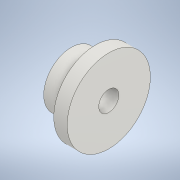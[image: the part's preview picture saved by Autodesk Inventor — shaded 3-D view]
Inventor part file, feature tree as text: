
AUTODESK INVENTOR PART (.ipt)
format: ipt  version: 2022.1 (Build 261234000, 234)  size: 116,224 bytes
history: native  units: mm
features: extrude x3, sketch x3
ambient origin geometry x8: Origin, YZ Plane, XZ Plane, XY Plane, X Axis, Y Axis, Z Axis, Center Point
bodies: Body1 (feature_tree)
feature tree (6):
  extrude  "Extrusión3"  Depth=28.0mm TaperAngle=0.0deg
  extrude  "Extrusión4"  Depth=18.0mm TaperAngle=0.0deg
  extrude  "Extrusión5"  TaperAngle=0.0deg  [1 undecoded]
  sketch  "Boceto3"  dims[d6=62.0mm d7=28.0mm d8=0.0mm]
  sketch  "Boceto4"  dims[d9=41.0mm d10=18.0mm d11=0.0mm]
  sketch  "Boceto5"  dims[d12=15.0mm d13=0.0mm d14=0.0mm]
note: 1 required parameter value undecoded (feature->parameter linkage not recoverable at this tier; creation-order binding heuristic only, values carry confidence <= 0.55)
